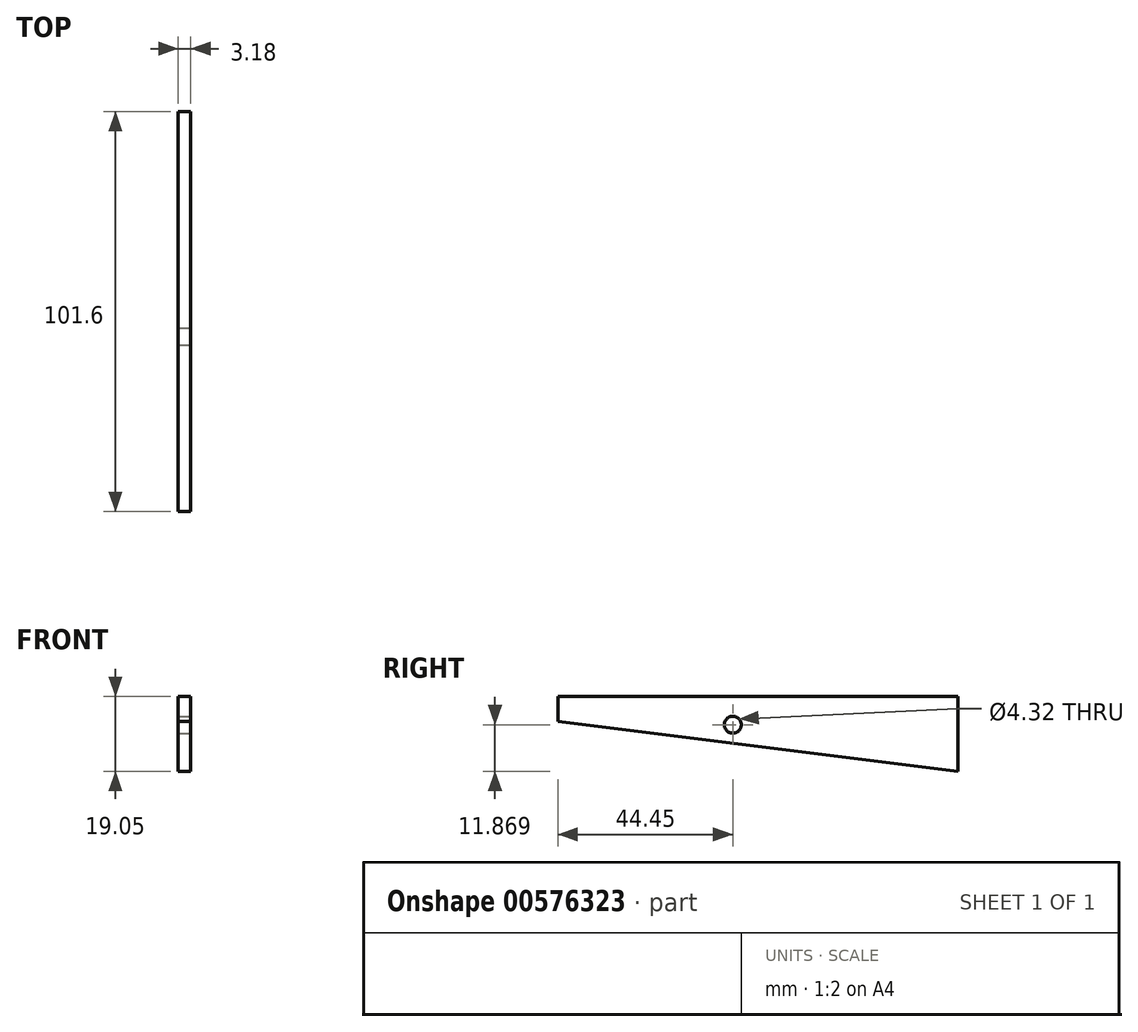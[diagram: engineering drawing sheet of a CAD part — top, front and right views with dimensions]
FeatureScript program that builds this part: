
annotation { "Feature Type Name" : "Feature", "Feature Type Description" : "" }
export const myFeature = defineFeature(function(context is Context, id is Id, definition is map)
    precondition{}
    {
        {
            var Q0;
            Q0=qCreatedBy(makeId("Right.planeOp"),FACE);
            var sketch = newSketch(context, id + "F0", { "sketchPlane" : qUnion([Q0])});
            skLineSegment(sketch, "E0", {"start": v(0, 0) * mm, "end": v(-101.6, 0) * mm});
            skLineSegment(sketch, "E1", {"start": v(-101.6, 0) * mm, "end": v(-101.6, 19.05) * mm});
            skLineSegment(sketch, "E2", {"start": v(-101.6, 19.05) * mm, "end": v(0, 19.05) * mm});
            skLineSegment(sketch, "E3", {"start": v(0, 19.05) * mm, "end": v(0, 0) * mm});
            skLineSegment(sketch, "E4", {"start": v(-101.6, 19.05) * mm, "end": v(-101.6, 12.7) * mm});
            skLineSegment(sketch, "E5", {"start": v(-101.6, 12.7) * mm, "end": v(0, 0) * mm});
            skSolve(sketch);
        }
        {
            var Q0;
            Q0=makeQuery(id+"F0.imprint","IMPRINT",FACE,{"disambiguationData":[TD([[makeQuery(id+"F0.imprint","IMPRINT",EDGE,{"derivedFrom":sQuery(id+"F0.wireOp",EDGE,"E2")}),-1.0]])]});
            extrude(context, id + "F1", {"entities" : qUnion([Q0]), "endBound" : BoundingType.SYMMETRIC, "depth" : 3.17 * mm, "offsetDistance" : 25.4 * mm});
        }
        {
            var Q0;
            Q0=makeQuery(id+"F1.opExtrude","CAP_FACE",FACE,{"disambiguationData":[OSD([sQuery(id+"F0.wireOp",EDGE,"E2"),sQuery(id+"F0.wireOp",EDGE,"E3"),sQuery(id+"F0.wireOp",EDGE,"E4"),sQuery(id+"F0.wireOp",EDGE,"E5")])],"isStart":false});
            var sketch = newSketch(context, id + "F2", { "sketchPlane" : qUnion([Q0])});
            skLineSegment(sketch, "E6", {"start": v(0, 19.05) * mm, "end": v(0, 11.87) * mm});
            skLineSegment(sketch, "E7", {"start": v(0, 11.87) * mm, "end": v(-57.15, 11.87) * mm});
            skSolve(sketch);
        }
        {
            var Q0;
            Q0=sQuery(id+"F2.wireOp",VERTEX,"E7.end");
            var Q1;
            Q1=makeQuery(id+"F1.opExtrude","SWEPT_BODY",BODY,{"disambiguationData":[OSD([sQuery(id+"F0.wireOp",EDGE,"E2"),sQuery(id+"F0.wireOp",EDGE,"E3"),sQuery(id+"F0.wireOp",EDGE,"E4"),sQuery(id+"F0.wireOp",EDGE,"E5")])]});
            hole(context, id + "F3", {"style" : HoleStyle.SIMPLE, "endStyle" : HoleEndStyle.BLIND, "standardTappedOrClearance" : lookupTablePath({ "standard" : "ANSI", "fit" : "Close", "size" : "#8", "type" : "Clearance" }), "standardBlindInLast" : lookupTablePath({ "fit" : "Close", "standard" : "ANSI", "size" : "#8", "type" : "Clearance" }), "holeDiameter" : 4.32 * mm, "holeDepth" : 762 * mm, "isTappedThrough" : true, "tappedDepth" : 12.7 * mm, "tapClearance" : 3, "locations" : qUnion([Q0]), "scope" : qUnion([Q1])});
        }
    });
